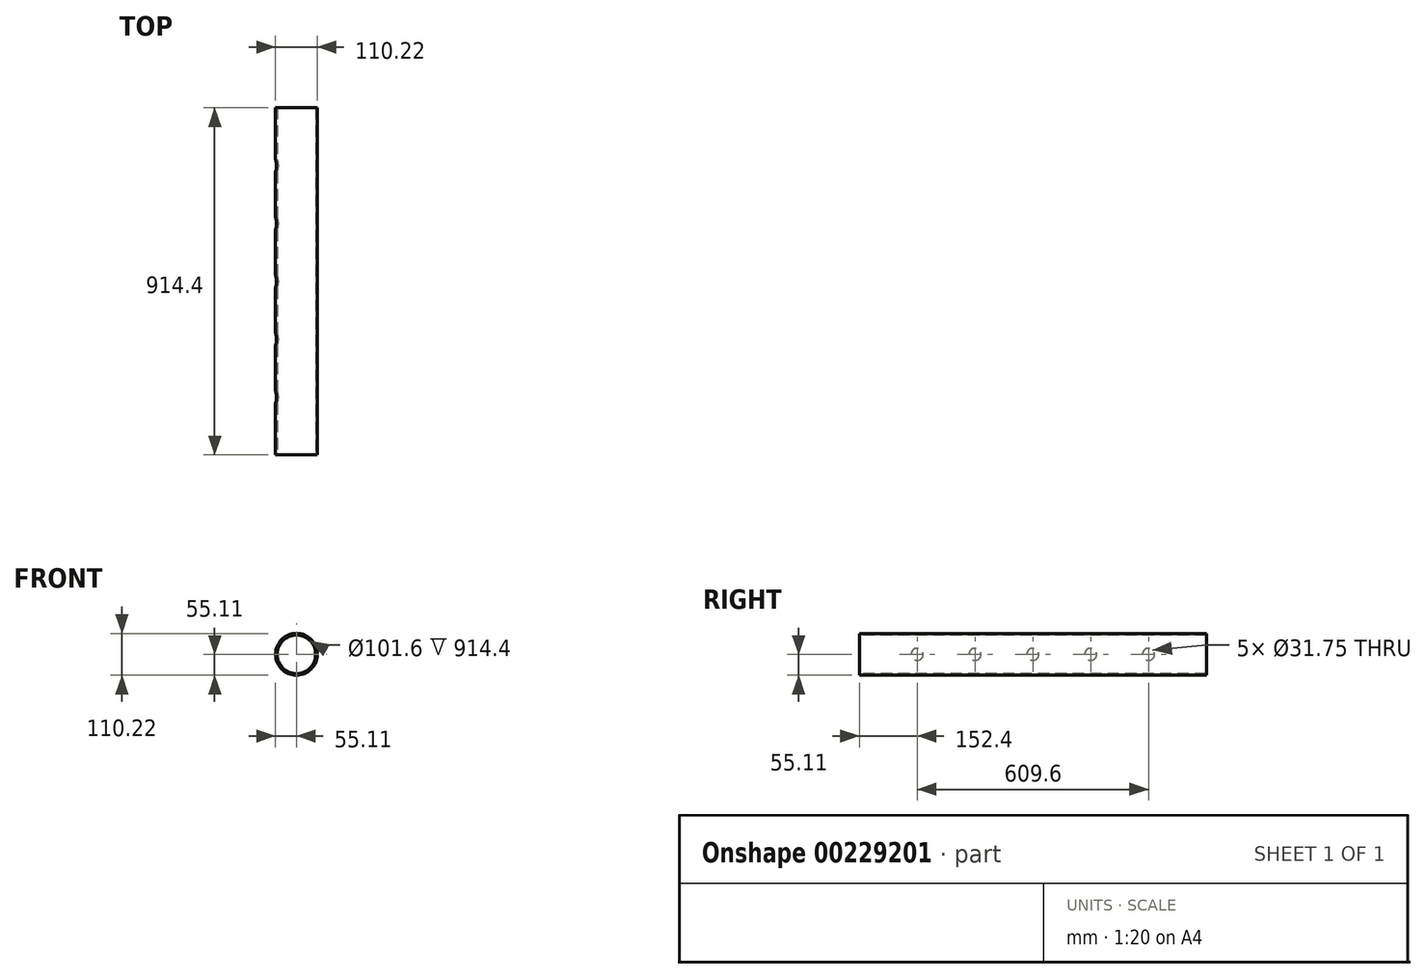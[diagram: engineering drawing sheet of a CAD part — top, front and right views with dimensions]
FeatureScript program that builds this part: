
annotation { "Feature Type Name" : "Feature", "Feature Type Description" : "" }
export const myFeature = defineFeature(function(context is Context, id is Id, definition is map)
    precondition{}
    {
        {
            var Q0;
            Q0=qCreatedBy(makeId("Front.planeOp"),FACE);
            var sketch = newSketch(context, id + "F0", { "sketchPlane" : qUnion([Q0])});
            skCircle(sketch, "E0", {"center": v(0, 0) * mm, "radius": 55.11 * mm});
            skSolve(sketch);
        }
        {
            var Q0;
            Q0 = qSketchRegion(id + "F0", true);
            extrude(context, id + "F1", {"entities" : qUnion([Q0]), "depth" : 914.4 * mm});
        }
        {
            var Q0;
            Q0=makeQuery(id+"F1.opExtrude","CAP_FACE",FACE,{"disambiguationData":[OSD([sQuery(id+"F0.wireOp",EDGE,"E0")])],"isStart":false});
            var sketch = newSketch(context, id + "F2", { "sketchPlane" : qUnion([Q0])});
            skPoint(sketch, "E1", {"position": v(0, 0) * mm});
            skSolve(sketch);
        }
        {
            var Q0;
            Q0=sQuery(id+"F2.wireOp",VERTEX,"E1");
            var Q1;
            Q1=makeQuery(id+"F1.opExtrude","SWEPT_BODY",BODY,{"disambiguationData":[OSD([sQuery(id+"F0.wireOp",EDGE,"E0")])]});
            hole(context, id + "F3", {"style" : HoleStyle.SIMPLE, "endStyle" : HoleEndStyle.THROUGH, "holeDiameter" : 101.6 * mm, "locations" : qUnion([Q0]), "scope" : qUnion([Q1]), "isTappedThrough" : true});
        }
        {
            var Q0;
            Q0=qCreatedBy(makeId("Right.planeOp"),FACE);
            var sketch = newSketch(context, id + "F4", { "sketchPlane" : qUnion([Q0])});
            skPoint(sketch, "E2", {"position": v(-457.2, 0) * mm});
            skPoint(sketch, "E3", {"position": v(-304.8, 0) * mm});
            skPoint(sketch, "E4", {"position": v(-152.4, 0) * mm});
            skPoint(sketch, "E5", {"position": v(-609.6, 0) * mm});
            skPoint(sketch, "E6", {"position": v(-762, 0) * mm});
            skSolve(sketch);
        }
        {
            var Q0;
            Q0=qCreatedBy(makeId("Right.planeOp"),FACE);
            var sketch = newSketch(context, id + "F5", { "sketchPlane" : qUnion([Q0])});
            skCircle(sketch, "E7", {"center": v(-762, 0) * mm, "radius": 15.88 * mm});
            skCircle(sketch, "E8", {"center": v(-609.6, 0) * mm, "radius": 15.88 * mm});
            skCircle(sketch, "E9", {"center": v(-457.2, 0) * mm, "radius": 15.88 * mm});
            skCircle(sketch, "E10", {"center": v(-304.8, 0) * mm, "radius": 15.88 * mm});
            skCircle(sketch, "E11", {"center": v(-152.4, 0) * mm, "radius": 15.88 * mm});
            skSolve(sketch);
        }
        {
            var Q0;
            Q0 = qSketchRegion(id + "F5", true);
            extrude(context, id + "F6", {"entities" : qUnion([Q0]), "operationType" : NewBodyOperationType.REMOVE, "oppositeDirection" : true, "depth" : 88.9 * mm});
        }
    });
